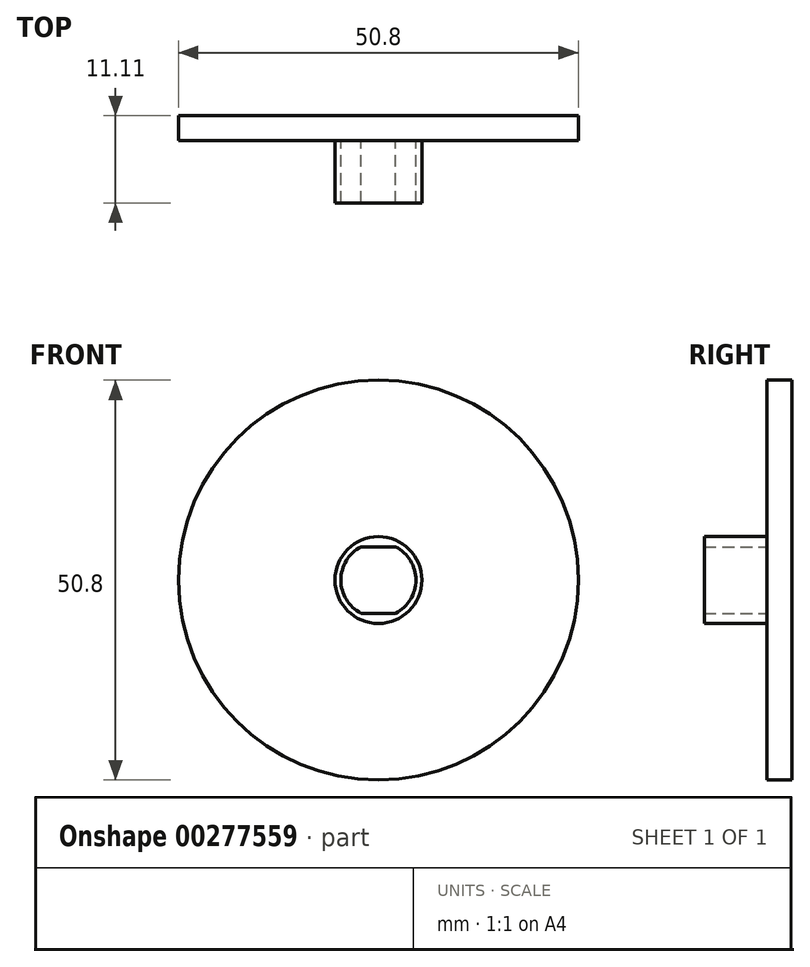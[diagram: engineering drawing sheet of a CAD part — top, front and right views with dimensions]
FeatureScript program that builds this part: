
annotation { "Feature Type Name" : "Feature", "Feature Type Description" : "" }
export const myFeature = defineFeature(function(context is Context, id is Id, definition is map)
    precondition{}
    {
        {
            var Q0;
            Q0=qCreatedBy(makeId("Front.planeOp"),FACE);
            var sketch = newSketch(context, id + "F0", { "sketchPlane" : qUnion([Q0])});
            skCircle(sketch, "E0", {"center": v(0, 0) * mm, "radius": 25.4 * mm});
            skSolve(sketch);
        }
        {
            var Q0;
            Q0=makeQuery(id+"F0.imprint","IMPRINT",FACE,{"disambiguationData":[TD([[makeQuery(id+"F0.imprint","IMPRINT",EDGE,{"derivedFrom":sQuery(id+"F0.wireOp",EDGE,"E0")}),1.0]])]});
            extrude(context, id + "F1", {"entities" : qUnion([Q0]), "depth" : 3.17 * mm});
        }
        {
            var Q0;
            Q0=makeQuery(id+"F1.opExtrude","CAP_FACE",FACE,{"disambiguationData":[OSD([sQuery(id+"F0.wireOp",EDGE,"E0")])],"isStart":false});
            var sketch = newSketch(context, id + "F2", { "sketchPlane" : qUnion([Q0])});
            skLineSegment(sketch, "E1", {"start": v(0, 3.97) * mm, "end": v(0, -3.97) * mm, "construction": true});
            skPoint(sketch, "E2", {"position": v(0, 0) * mm});
            skLineSegment(sketch, "E3", {"start": v(-4.76, 0) * mm, "end": v(4.76, 0) * mm, "construction": true});
            skArc(sketch, "E4", {"start": v(-2.2, 4.22) * mm, "mid": v(-4.76, 0) * mm, "end": v(-2.2, -4.22) * mm});
            skLineSegment(sketch, "E5", {"start": v(-2.63, 3.97) * mm, "end": v(2.63, 3.97) * mm});
            skLineSegment(sketch, "E6", {"start": v(-2.63, -3.97) * mm, "end": v(2.63, -3.97) * mm});
            skCircle(sketch, "E7", {"center": v(0, 0) * mm, "radius": 5.52 * mm});
            skLineSegment(sketch, "E8", {"start": v(2.2, 4.22) * mm, "end": v(-2.2, 4.22) * mm});
            skLineSegment(sketch, "E9", {"start": v(-2.2, -4.22) * mm, "end": v(2.2, -4.22) * mm});
            skArc(sketch, "E10.trimOffspring", {"start": v(2.2, -4.22) * mm, "mid": v(4.76, 0) * mm, "end": v(2.2, 4.22) * mm});
            skSolve(sketch);
        }
        {
            var Q0;
            Q0=makeQuery(id+"F2.imprint","IMPRINT",FACE,{"disambiguationData":[TD([[makeQuery(id+"F2.imprint","IMPRINT",EDGE,{"derivedFrom":sQuery(id+"F2.wireOp",EDGE,"E7")}),1.0]])]});
            extrude(context, id + "F3", {"entities" : qUnion([Q0]), "operationType" : NewBodyOperationType.ADD, "depth" : 7.94 * mm});
        }
    });
